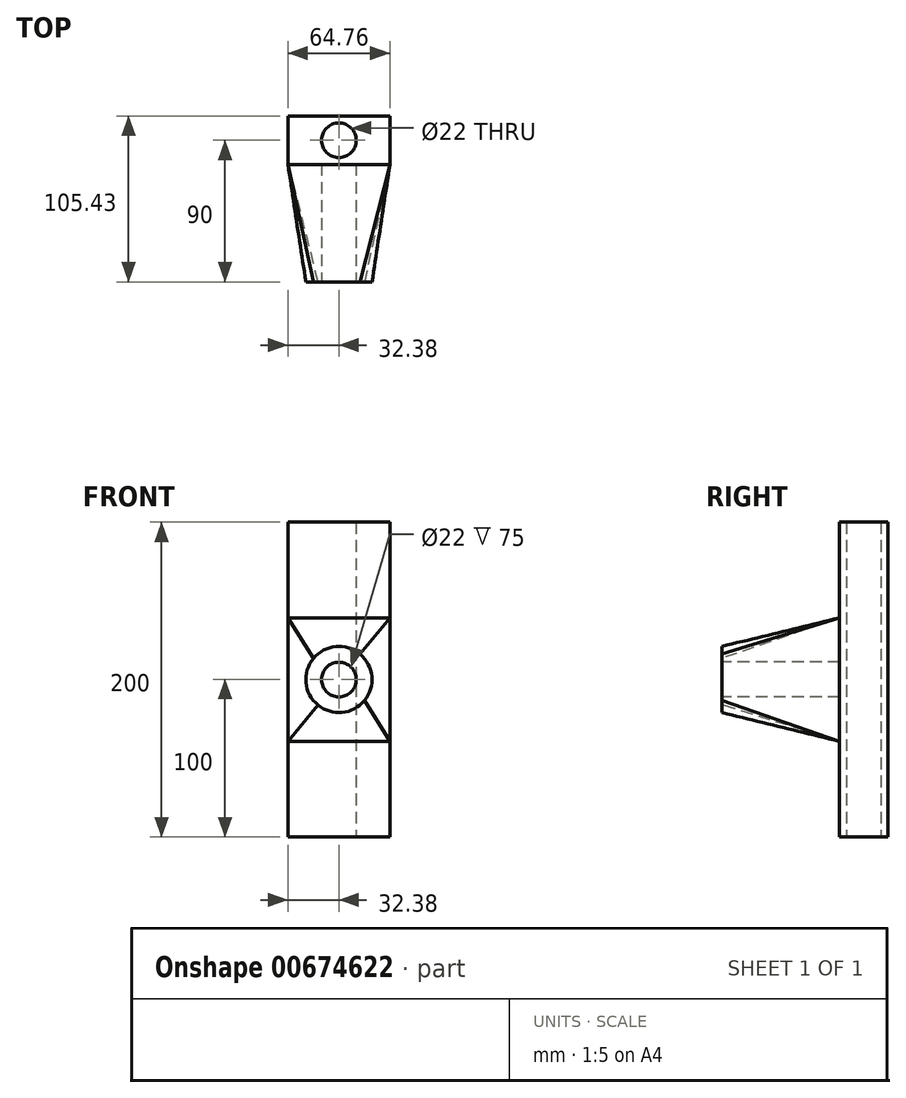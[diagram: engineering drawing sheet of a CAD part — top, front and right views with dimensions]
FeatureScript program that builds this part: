
annotation { "Feature Type Name" : "Feature", "Feature Type Description" : "" }
export const myFeature = defineFeature(function(context is Context, id is Id, definition is map)
    precondition{}
    {
        {
            var Q0;
            Q0=qCreatedBy(makeId("Top.planeOp"),FACE);
            var sketch = newSketch(context, id + "F0", { "sketchPlane" : qUnion([Q0])});
            skCircle(sketch, "E0", {"center": v(0, 0) * mm, "radius": 11 * mm});
            skLineSegment(sketch, "E1.bottom", {"start": v(32.38, 15.43) * mm, "end": v(-32.38, 15.43) * mm});
            skLineSegment(sketch, "E1.top", {"start": v(32.38, -15.43) * mm, "end": v(-32.38, -15.43) * mm});
            skLineSegment(sketch, "E1.left", {"start": v(32.38, 15.43) * mm, "end": v(32.38, -15.43) * mm});
            skLineSegment(sketch, "E1.right", {"start": v(-32.38, 15.43) * mm, "end": v(-32.38, -15.43) * mm});
            skSolve(sketch);
        }
        {
            var Q0;
            Q0=makeQuery(id+"F0.imprint","IMPRINT",FACE,{"disambiguationData":[TD([[makeQuery(id+"F0.imprint","IMPRINT",EDGE,{"derivedFrom":sQuery(id+"F0.wireOp",EDGE,"E0")}),-1.0]])]});
            extrude(context, id + "F1", {"entities" : qUnion([Q0]), "endBound" : BoundingType.SYMMETRIC, "depth" : 200 * mm, "offsetDistance" : 25 * mm});
        }
        {
            var Q0;
            Q0=qCreatedBy(makeId("Front.planeOp"),FACE);
            cPlane(context, id + "F2", {"entities" : qUnion([Q0]), "cplaneType" : CPlaneType.OFFSET, "offset" : 90 * mm, "width" : 150 * mm, "height" : 150 * mm});
        }
        {
            var Q0;
            Q0=qCreatedBy(id+"F2.planeOp",FACE);
            var sketch = newSketch(context, id + "F3", { "sketchPlane" : qUnion([Q0])});
            skCircle(sketch, "E2", {"center": v(0, 0) * mm, "radius": 21 * mm});
            skSolve(sketch);
        }
        {
            var Q0;
            Q0=makeQuery(id+"F1.opExtrude","SWEPT_FACE",FACE,{"disambiguationData":[OSD([sQuery(id+"F0.wireOp",EDGE,"E1.top")])]});
            var sketch = newSketch(context, id + "F4", { "sketchPlane" : qUnion([Q0])});
            skLineSegment(sketch, "E3.bottom", {"start": v(32.38, 39.2) * mm, "end": v(-32.38, 39.2) * mm});
            skLineSegment(sketch, "E3.top", {"start": v(32.38, -39.2) * mm, "end": v(-32.38, -39.2) * mm});
            skLineSegment(sketch, "E3.left", {"start": v(32.38, 39.2) * mm, "end": v(32.38, -39.2) * mm});
            skLineSegment(sketch, "E3.right", {"start": v(-32.38, 39.2) * mm, "end": v(-32.38, -39.2) * mm});
            skPoint(sketch, "E3.middle", {"position": v(0, 0) * mm});
            skSolve(sketch);
        }
        {
            var Q1;
            Q1=makeQuery(id+"F4.imprint","IMPRINT",FACE,{"disambiguationData":[TD([[makeQuery(id+"F4.imprint","IMPRINT",EDGE,{"derivedFrom":sQuery(id+"F4.wireOp",EDGE,"E3.bottom")}),1.0]])]});
            var Q2;
            Q2=makeQuery(id+"F3.imprint","IMPRINT",FACE,{"disambiguationData":[TD([[makeQuery(id+"F3.imprint","IMPRINT",EDGE,{"derivedFrom":sQuery(id+"F3.wireOp",EDGE,"E2")}),1.0]])]});
            loft(context, id + "F5", {"operationType" : NewBodyOperationType.ADD, "sheetProfilesArray" : [{ "sheetProfileEntities" : qUnion([Q1]) }, { "sheetProfileEntities" : qUnion([Q2]) }]});
        }
        {
            var Q0;
            Q0=makeQuery(id+"F5.opLoft","CAP_FACE",FACE,{"disambiguationData":[OSD([makeQuery(id+"F3.imprint","IMPRINT",FACE,{"disambiguationData":[TD([[makeQuery(id+"F3.imprint","IMPRINT",EDGE,{"derivedFrom":sQuery(id+"F3.wireOp",EDGE,"E2")}),1.0]])]})])],"isStart":true});
            var sketch = newSketch(context, id + "F6", { "sketchPlane" : qUnion([Q0])});
            skCircle(sketch, "E4", {"center": v(0, 0) * mm, "radius": 11 * mm});
            skSolve(sketch);
        }
        {
            var Q0;
            Q0 = qSketchRegion(id + "F6", true);
            extrude(context, id + "F7", {"entities" : qUnion([Q0]), "operationType" : NewBodyOperationType.REMOVE, "oppositeDirection" : true, "depth" : 75 * mm, "offsetDistance" : 25 * mm});
        }
    });
